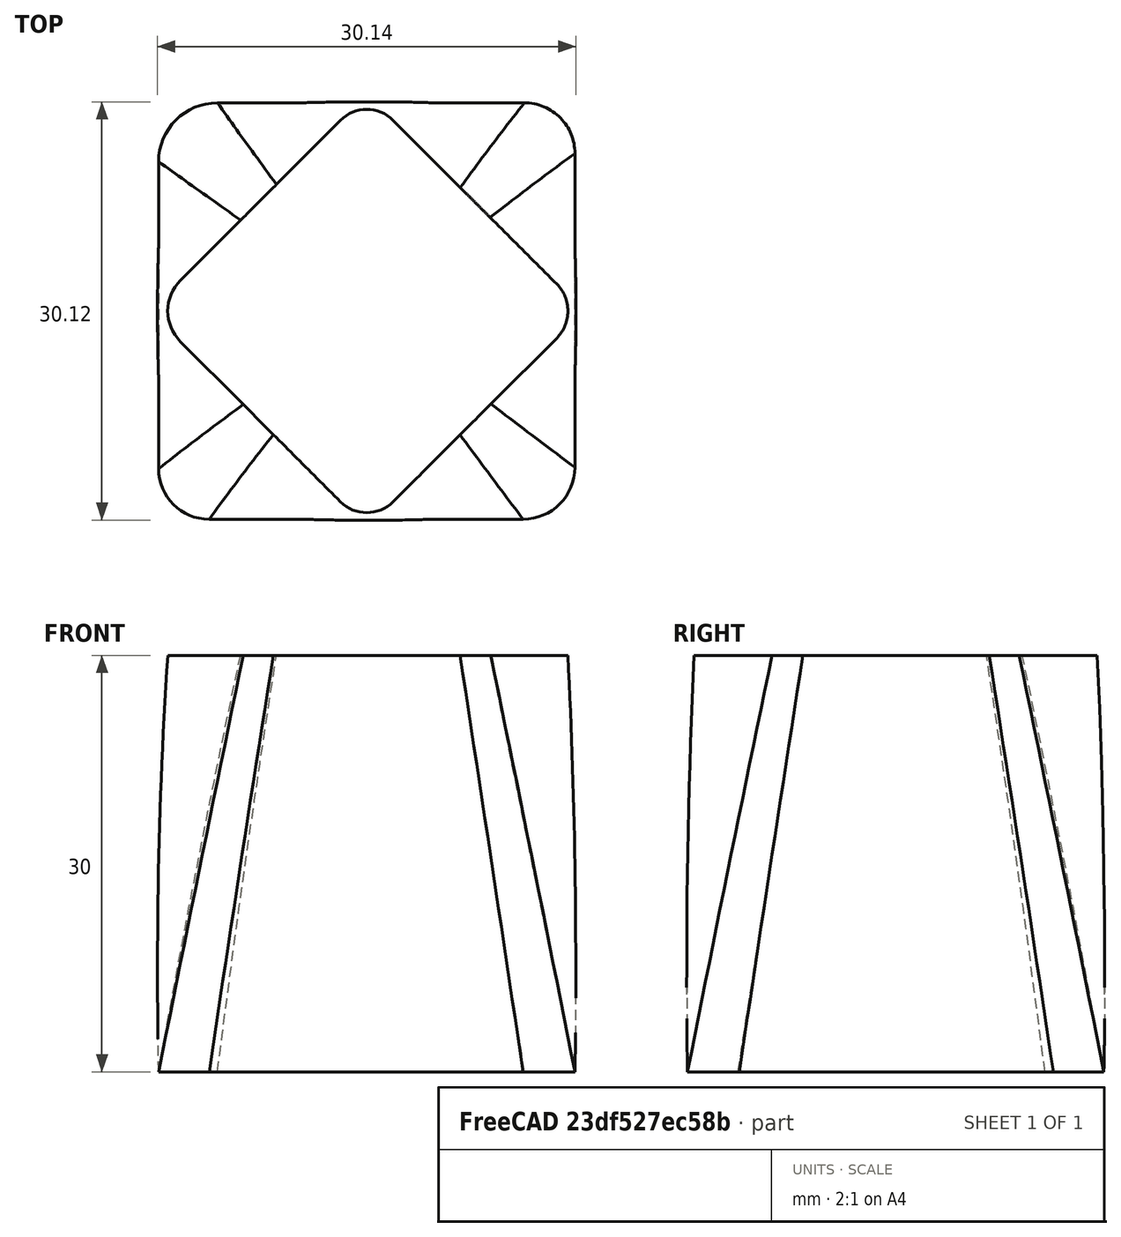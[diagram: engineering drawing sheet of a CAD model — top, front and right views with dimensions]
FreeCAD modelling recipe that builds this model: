
FCSTD DOCUMENT  (FreeCAD 0.20R27319 (Git))
Label: Twisted
License: All rights reserved
LicenseURL: http://en.wikipedia.org/wiki/All_rights_reserved
objects: Sketcher::SketchObject×3, PartDesign::AdditiveLoft×1, PartDesign::Body×1
note: 6 computed .brp shape members not serialized (recipe doc carries the construction recipe); baked Part::Feature solids carry a one-line shape summary decoded from their .brp

FEATURE [Sketcher::SketchObject] Sketch
  AttachmentOffset = pos=(0,0,-10) rot=(0,0,1;0rad)
  FullyConstrained = false
  MapMode = 5
  Placement = pos=(0,0,-10) rot=(0,0,1;0rad)
  Support = -> [XY_Plane]
  sketch-geometry (13):
    g0: LineSegment StartX=-15 StartY=10.7574 StartZ=0 EndX=-15 EndY=-11.3574 EndZ=0
    g1: LineSegment StartX=-11.3574 StartY=-15 StartZ=0 EndX=11.2725 EndY=-15 EndZ=0
    g2: LineSegment StartX=15 StartY=-11.2725 StartZ=0 EndX=15 EndY=11.3574 EndZ=0
    g3: LineSegment StartX=11.3574 StartY=15 StartZ=0 EndX=-10.7574 EndY=15 EndZ=0
    g4: GeomPoint X=0 Y=0 Z=0
    g5: ArcOfCircle CenterX=-10.7574 CenterY=10.7574 CenterZ=0 NormalX=0 NormalY=0 NormalZ=1 AngleXU=0 Radius=4.24264 StartAngle=1.5708 EndAngle=3.14159
    g6: GeomPoint X=-15 Y=15 Z=0
    g7: ArcOfCircle CenterX=11.3574 CenterY=11.3574 CenterZ=0 NormalX=0 NormalY=0 NormalZ=1 AngleXU=0 Radius=3.64264 StartAngle=0 EndAngle=1.5708
    g8: GeomPoint X=15 Y=15 Z=0
    g9: ArcOfCircle CenterX=11.2725 CenterY=-11.2725 CenterZ=0 NormalX=0 NormalY=0 NormalZ=1 AngleXU=0 Radius=3.72749 StartAngle=4.71239 EndAngle=6.28319
    g10: GeomPoint X=15 Y=-15 Z=0
    g11: ArcOfCircle CenterX=-11.3574 CenterY=-11.3574 CenterZ=0 NormalX=0 NormalY=0 NormalZ=1 AngleXU=0 Radius=3.64264 StartAngle=3.14159 EndAngle=4.71239
    g12: GeomPoint X=-15 Y=-15 Z=0
  constraints (23):
    c: Horizontal(g1)
    c: Horizontal(g3)
    c: Vertical(g0)
    c: Vertical(g2)
    c: Symmetric(g10,g6,g4)
    c: Coincident(g4,g-1)
    c: Distance(g8,g6) = 30
    c: PointOnObject(g6,g0)
    c: PointOnObject(g6,g3)
    c: Tangent(g0,g5) = -1.5708
    c: Tangent(g3,g5) = -1.5708
    c: PointOnObject(g8,g2)
    c: PointOnObject(g8,g3)
    c: Tangent(g2,g7) = -1.5708
    c: Tangent(g3,g7) = -1.5708
    c: PointOnObject(g10,g1)
    c: PointOnObject(g10,g2)
    c: Tangent(g1,g9) = -1.5708
    c: Tangent(g2,g9) = -1.5708
    c: PointOnObject(g12,g0)
    c: PointOnObject(g12,g1)
    c: Tangent(g0,g11) = -1.5708
    c: Tangent(g1,g11) = -1.5708
FEATURE [Sketcher::SketchObject] Sketch001
  AttachmentOffset = pos=(0,0,20) rot=(0,0,1;0.785398rad)
  ExternalGeometry = -> [Sketch]
  FullyConstrained = false
  MapMode = 5
  Placement = pos=(0,0,20) rot=(0,0,1;0.785398rad)
  Support = -> [XY_Plane]
  sketch-geometry (13):
    g0: LineSegment StartX=-11.0574 StartY=7.92987 StartZ=0 EndX=-11.0574 EndY=-8.37216 EndZ=0
    g1: LineSegment StartX=-8.37216 StartY=-11.0574 StartZ=0 EndX=8.30961 EndY=-11.0574 EndZ=0
    g2: LineSegment StartX=11.0574 StartY=-8.30961 StartZ=0 EndX=11.0574 EndY=8.37216 EndZ=0
    g3: LineSegment StartX=8.37216 StartY=11.0574 StartZ=0 EndX=-7.92987 EndY=11.0574 EndZ=0
    g4: GeomPoint X=0 Y=0 Z=0
    g5: ArcOfCircle CenterX=-7.92987 CenterY=7.92987 CenterZ=0 NormalX=0 NormalY=0 NormalZ=1 AngleXU=0 Radius=3.12749 StartAngle=1.5708 EndAngle=3.14159
    g6: GeomPoint X=-11.0574 Y=11.0574 Z=0
    g7: ArcOfCircle CenterX=-8.37216 CenterY=-8.37216 CenterZ=0 NormalX=0 NormalY=0 NormalZ=1 AngleXU=0 Radius=2.6852 StartAngle=3.14159 EndAngle=4.71239
    g8: GeomPoint X=-11.0574 Y=-11.0574 Z=0
    g9: ArcOfCircle CenterX=8.30961 CenterY=-8.30961 CenterZ=0 NormalX=0 NormalY=0 NormalZ=1 AngleXU=0 Radius=2.74775 StartAngle=4.71239 EndAngle=6.28319
    g10: GeomPoint X=11.0574 Y=-11.0574 Z=0
    g11: ArcOfCircle CenterX=8.37216 CenterY=8.37216 CenterZ=0 NormalX=0 NormalY=0 NormalZ=1 AngleXU=0 Radius=2.6852 StartAngle=0 EndAngle=1.5708
    g12: GeomPoint X=11.0574 Y=11.0574 Z=0
  constraints (22):
    c: Horizontal(g1)
    c: Horizontal(g3)
    c: Vertical(g0)
    c: Vertical(g2)
    c: Symmetric(g10,g6,g4)
    c: Coincident(g4,g-1)
    c: PointOnObject(g6,g0)
    c: PointOnObject(g6,g3)
    c: Tangent(g0,g5) = -1.5708
    c: Tangent(g3,g5) = -1.5708
    c: PointOnObject(g8,g0)
    c: PointOnObject(g8,g1)
    c: Tangent(g0,g7) = -1.5708
    c: Tangent(g1,g7) = -1.5708
    c: PointOnObject(g10,g1)
    c: PointOnObject(g10,g2)
    c: Tangent(g1,g9) = -1.5708
    c: Tangent(g2,g9) = -1.5708
    c: PointOnObject(g12,g2)
    c: PointOnObject(g12,g3)
    c: Tangent(g2,g11) = -1.5708
    c: Tangent(g3,g11) = -1.5708
FEATURE [Sketcher::SketchObject] Sketch002
  AttachmentOffset = pos=(0,0,5) rot=(0,0,1;0.785398rad)
  ExternalGeometry = -> [Sketch]
  FullyConstrained = true
  MapMode = 5
  Placement = pos=(0,0,5) rot=(0,0,1;0.785398rad)
  Support = -> [XY_Plane]
  sketch-geometry (2):
    g0: GeomPoint X=0 Y=0 Z=0
    g1: Circle CenterX=0 CenterY=0 CenterZ=0 NormalX=0 NormalY=0 NormalZ=1 AngleXU=0 Radius=15
  constraints (3):
    c: Coincident(g0,g-1)
    c: Coincident(g1,g0)
    c: Tangent(g1,g-3)
FEATURE [PartDesign::AdditiveLoft] AdditiveLoft
  Closed = false
  Profile = -> Sketch
  Ruled = false
  Sections = -> [Sketch002,Sketch001]
FEATURE [PartDesign::Body] Body
  Group = -> [Sketch,Sketch001,Sketch002,AdditiveLoft]
  Origin = -> Origin
  Tip = -> AdditiveLoft
